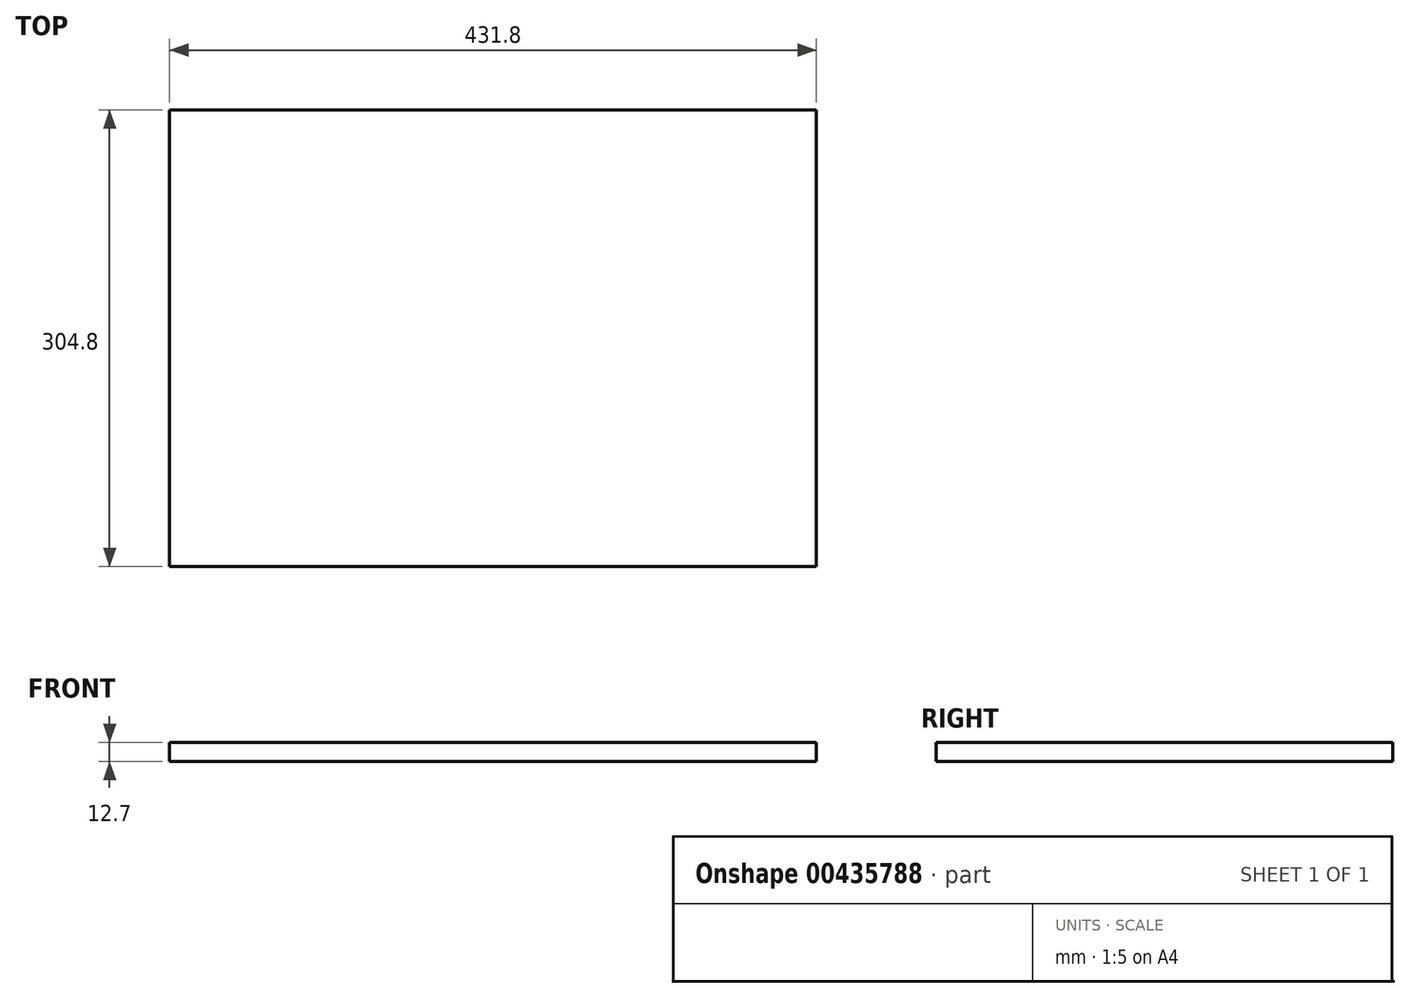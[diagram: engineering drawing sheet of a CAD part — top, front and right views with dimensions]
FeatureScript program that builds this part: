
annotation { "Feature Type Name" : "Feature", "Feature Type Description" : "" }
export const myFeature = defineFeature(function(context is Context, id is Id, definition is map)
    precondition{}
    {
        {
            var Q0;
            Q0=qCreatedBy(makeId("Top.planeOp"),FACE);
            var sketch = newSketch(context, id + "F0", { "sketchPlane" : qUnion([Q0])});
            skLineSegment(sketch, "E0.bottom", {"start": v(215.9, -152.4) * mm, "end": v(-215.9, -152.4) * mm});
            skLineSegment(sketch, "E0.top", {"start": v(215.9, 152.4) * mm, "end": v(-215.9, 152.4) * mm});
            skLineSegment(sketch, "E0.left", {"start": v(215.9, -152.4) * mm, "end": v(215.9, 152.4) * mm});
            skLineSegment(sketch, "E0.right", {"start": v(-215.9, -152.4) * mm, "end": v(-215.9, 152.4) * mm});
            skPoint(sketch, "E0.middle", {"position": v(0, 0) * mm});
            skSolve(sketch);
        }
        {
            var Q0;
            Q0=makeQuery(id+"F0.imprint","IMPRINT",FACE,{"disambiguationData":[TD([[makeQuery(id+"F0.imprint","IMPRINT",EDGE,{"derivedFrom":sQuery(id+"F0.wireOp",EDGE,"E0.bottom")}),-1.0]])]});
            extrude(context, id + "F1", {"entities" : qUnion([Q0]), "depth" : 12.7 * mm});
        }
    });
